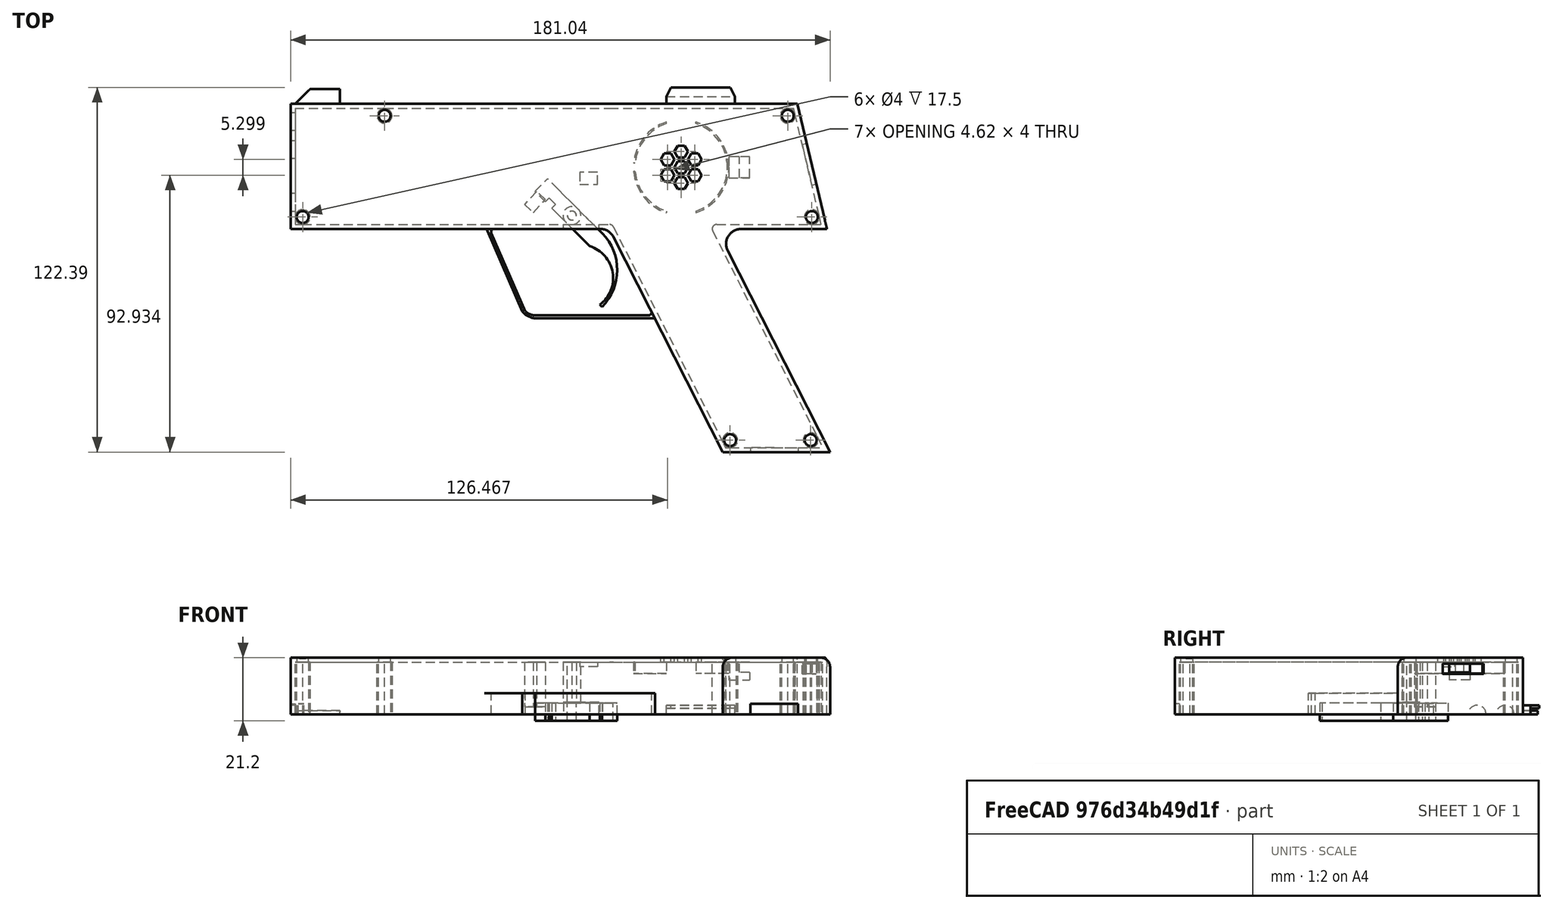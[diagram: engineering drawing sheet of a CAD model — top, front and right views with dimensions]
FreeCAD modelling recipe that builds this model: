
FCSTD DOCUMENT  (FreeCAD 0.21R33771 (Git))
Label: TaggerPart1
License: All rights reserved
LicenseURL: http://en.wikipedia.org/wiki/All_rights_reserved
objects: Sketcher::SketchObject×24, PartDesign::Pad×12, PartDesign::Pocket×12, PartDesign::Fillet×4, PartDesign::Body×2, PartDesign::Thickness×1, PartDesign::Hole×1, Part::Compound×1, App::MeasureDistance×1, App::Part×1
note: 87 computed .brp shape members not serialized (recipe doc carries the construction recipe); baked Part::Feature solids carry a one-line shape summary decoded from their .brp

FEATURE [Sketcher::SketchObject] Sketch
  FullyConstrained = false
  MapMode = 5
  Support = -> [XY_Plane]
  sketch-geometry (12):
    g0: LineSegment StartX=0 StartY=0 StartZ=0 EndX=107 EndY=0 EndZ=0
    g1: LineSegment StartX=0 StartY=0 StartZ=0 EndX=0 EndY=-42 EndZ=0
    g2: LineSegment StartX=0 StartY=-42 StartZ=0 EndX=107 EndY=-42 EndZ=0
    g3: LineSegment StartX=107 StartY=0 StartZ=0 EndX=107 EndY=-42 EndZ=0
    g4: LineSegment StartX=107 StartY=0 StartZ=0 EndX=170 EndY=0 EndZ=0
    g5: LineSegment StartX=107 StartY=-42 StartZ=0 EndX=143 EndY=-42 EndZ=0
    g6: LineSegment StartX=107 StartY=-42 StartZ=0 EndX=145.042 EndY=-116.892 EndZ=0
    g7: LineSegment StartX=143 StartY=-42 StartZ=0 EndX=181.042 EndY=-116.892 EndZ=0
    g8: LineSegment StartX=145.042 StartY=-116.892 StartZ=0 EndX=181.042 EndY=-116.892 EndZ=0
    g9: LineSegment StartX=143 StartY=-42 StartZ=0 EndX=180 EndY=-42 EndZ=0
    g10: LineSegment StartX=180 StartY=-42 StartZ=0 EndX=170 EndY=0 EndZ=0
    g11: LineSegment StartX=170 StartY=0 StartZ=0 EndX=170 EndY=-42 EndZ=0
  constraints (32):
    c: Coincident(g0,g-1)
    c: PointOnObject(g0,g-1)
    c: Coincident(g1,g0)
    c: PointOnObject(g1,g-2)
    c: Coincident(g2,g1)
    c: Horizontal(g2)
    c: Coincident(g3,g0)
    c: Coincident(g3,g2)
    c: Vertical(g3)
    c: Coincident(g4,g0)
    c: PointOnObject(g4,g-1)
    c: Coincident(g5,g2)
    c: Horizontal(g5)
    c: Coincident(g6,g2)
    c: Coincident(g7,g5)
    c: Coincident(g8,g6)
    c: Coincident(g8,g7)
    c: Horizontal(g8)
    c: Coincident(g9,g7)
    c: Horizontal(g9)
    c: Coincident(g10,g9)
    c: Coincident(g10,g4)
    c: Coincident(g11,g4)
    c: PointOnObject(g11,g9)
    c: Vertical(g11)
    c: DistanceY(g1,g1) = 42
    c: DistanceX(g1,g9) = 180
    c: DistanceX(g0,g4) = 170
    c: Parallel(g7,g6)
    c: Distance(g7) = 84
    c: DistanceX(g5,g5) = 36
    c: DistanceX(g9,g9) = 37
FEATURE [Sketcher::SketchObject] Sketch001  label="Triggerumrahmung"
  ExternalGeometry = -> [Sketch]
  FullyConstrained = false
  MapMode = 5
  Support = -> [XY_Plane]
  sketch-geometry (16):
    g0: LineSegment StartX=107 StartY=-42 StartZ=0 EndX=107 EndY=-71 EndZ=0
    g1: LineSegment StartX=107 StartY=-71 StartZ=0 EndX=121.731 EndY=-71 EndZ=0
    g2: LineSegment StartX=107 StartY=-71 StartZ=0 EndX=66.7308 EndY=-71 EndZ=0
    g3: LineSegment StartX=66.7308 StartY=-71 StartZ=0 EndX=66.7308 EndY=-42 EndZ=0
    g4: LineSegment StartX=121.731 StartY=-71 StartZ=0 EndX=81.9929 EndY=-71 EndZ=0
    g5: LineSegment StartX=78.7821 StartY=-69.7248 StartZ=0 EndX=66.7308 EndY=-42 EndZ=0
    g6: ArcOfCircle CenterX=82.1691 CenterY=-65.8766 CenterZ=0 NormalX=0 NormalY=0 NormalZ=1 AngleXU=0 Radius=5.12641 StartAngle=3.99065 EndAngle=4.678
    g7: LineSegment StartX=121.731 StartY=-71 StartZ=0 EndX=121.731 EndY=-72 EndZ=0
    g8: LineSegment StartX=121.731 StartY=-72 StartZ=0 EndX=81.9929 EndY=-72 EndZ=0
    g9: LineSegment StartX=81.9929 StartY=-71 StartZ=0 EndX=81.9929 EndY=-72 EndZ=0
    g10: ArcOfCircle CenterX=82.7291 CenterY=-65.6034 CenterZ=0 NormalX=0 NormalY=0 NormalZ=1 AngleXU=0 Radius=6.43882 StartAngle=3.8362 EndAngle=4.59779
    g11: LineSegment StartX=66.7308 StartY=-42 StartZ=0 EndX=65.7308 EndY=-42 EndZ=0
    g12: LineSegment StartX=65.7308 StartY=-42 StartZ=0 EndX=77.7821 EndY=-69.7248 EndZ=0
    g13: LineSegment StartX=78.7821 StartY=-69.7248 StartZ=0 EndX=77.7821 EndY=-69.7248 EndZ=0
    g14: LineSegment StartX=121.731 StartY=-72 StartZ=0 EndX=122.239 EndY=-72 EndZ=0
    g15: LineSegment StartX=122.239 StartY=-72 StartZ=0 EndX=121.731 EndY=-71 EndZ=0
  constraints (44):
    c: Coincident(g0,g-4)
    c: Vertical(g0)
    c: DistanceY(g0,g0) = 29
    c: PointOnObject(g1,g-3)
    c: Horizontal(g1)
    c: Coincident(g1,g0)
    c: Coincident(g2,g0)
    c: Horizontal(g2)
    c: DistanceX(g2,g1) = 55
    c: Coincident(g3,g2)
    c: PointOnObject(g3,g-4)
    c: Vertical(g3)
    c: Coincident(g4,g1)
    c: Coincident(g5,g3)
    c: Horizontal(g4)
    c: Coincident(g6,g5)
    c: Coincident(g6,g4)
    c: Coincident(g7,g4)
    c: Vertical(g7)
    c: Coincident(g8,g7)
    c: Horizontal(g8)
    c: Coincident(g9,g4)
    c: Coincident(g9,g8)
    c: Vertical(g9)
    c: DistanceY(g9,g9) = 1
    c: Coincident(g10,g8)
    c: Coincident(g11,g5)
    c: PointOnObject(g11,g-4)
    c: DistanceX(g11,g11) = 1
    c: Coincident(g12,g11)
    c: Coincident(g12,g10)
    c: DistanceX(g6) = 82.1691
    c: DistanceY(g6) = -65.8766
    c: Equal(g12,g5)
    c: Coincident(g13,g5)
    c: Horizontal(g13)
    c: Coincident(g10,g13)
    c: DistanceX(g4) = 81.9929
    c: DistanceX(g5) = 78.7821
    c: Coincident(g14,g8)
    c: PointOnObject(g14,g-3)
    c: Horizontal(g14)
    c: Coincident(g15,g14)
    c: Coincident(g15,g4)
FEATURE [Sketcher::SketchObject] Sketch002  label="Kim2"
  AttachmentOffset = pos=(0,0,2) rot=(0,0,1;0rad)
  ExternalGeometry = -> [Sketch]
  FullyConstrained = false
  MapMode = 5
  Placement = pos=(0,0,2) rot=(0,0,1;0rad)
  Support = -> [XY_Plane]
  sketch-geometry (10):
    g0: LineSegment StartX=170 StartY=0 StartZ=0 EndX=170 EndY=-42 EndZ=0
    g1: LineSegment StartX=149.115 StartY=0 StartZ=0 EndX=149.115 EndY=2.5 EndZ=0
    g2: LineSegment StartX=149.115 StartY=2.5 StartZ=0 EndX=147.523 EndY=5.5 EndZ=0
    g3: LineSegment StartX=147.523 StartY=5.5 StartZ=0 EndX=127.662 EndY=5.5 EndZ=0
    g4: LineSegment StartX=127.662 StartY=5.5 StartZ=0 EndX=126.07 EndY=2.5 EndZ=0
    g5: LineSegment StartX=126.07 StartY=2.5 StartZ=0 EndX=126.07 EndY=0 EndZ=0
    g6: LineSegment StartX=126.07 StartY=2.5 StartZ=0 EndX=149.115 EndY=2.5 EndZ=0
    g7: LineSegment StartX=127.662 StartY=5.5 StartZ=0 EndX=127.662 EndY=2.5 EndZ=0
    g8: LineSegment StartX=147.523 StartY=5.5 StartZ=0 EndX=147.523 EndY=2.5 EndZ=0
    g9: LineSegment StartX=126.07 StartY=0 StartZ=0 EndX=149.115 EndY=0 EndZ=0
  constraints (26):
    c: Coincident(g0,g-6)
    c: PointOnObject(g0,g-7)
    c: Vertical(g0)
    c: PointOnObject(g1,g-4)
    c: Vertical(g1)
    c: Coincident(g3,g2)
    c: Horizontal(g3)
    c: Coincident(g4,g3)
    c: Coincident(g5,g4)
    c: PointOnObject(g5,g-4)
    c: Equal(g5,g1)
    c: Equal(g4,g2)
    c: Coincident(g2,g1)
    c: Vertical(g5)
    c: Coincident(g6,g4)
    c: Coincident(g6,g1)
    c: Coincident(g7,g3)
    c: PointOnObject(g7,g6)
    c: Vertical(g7)
    c: Coincident(g8,g2)
    c: PointOnObject(g8,g6)
    c: Vertical(g8)
    c: DistanceY(g8,g8) = 3
    c: DistanceY(g5,g3) = 5.5
    c: Coincident(g9,g5)
    c: Coincident(g9,g1)
FEATURE [Sketcher::SketchObject] Sketch003  label="Korn"
  ExternalGeometry = -> [Sketch,Sketch002]
  FullyConstrained = false
  MapMode = 5
  Support = -> [XY_Plane]
  sketch-geometry (7):
    g0: LineSegment StartX=1.52333 StartY=0 StartZ=0 EndX=6.52333 EndY=5 EndZ=0
    g1: LineSegment StartX=6.52333 StartY=5 StartZ=0 EndX=16.5233 EndY=5 EndZ=0
    g2: LineSegment StartX=16.5233 StartY=5 StartZ=0 EndX=16.5233 EndY=0 EndZ=0
    g3: LineSegment StartX=16.5233 StartY=0 StartZ=0 EndX=1.52333 EndY=0 EndZ=0
    g4: LineSegment StartX=127.662 StartY=5.5 StartZ=0 EndX=127.662 EndY=0 EndZ=0
    g5: LineSegment StartX=6.52333 StartY=5 StartZ=0 EndX=6.52333 EndY=0 EndZ=0
    g6: LineSegment StartX=1.52333 StartY=0 StartZ=0 EndX=1.52333 EndY=-1.50251 EndZ=0
  constraints (19):
    c: Coincident(g1,g0)
    c: Horizontal(g1)
    c: Coincident(g2,g1)
    c: PointOnObject(g2,g-3)
    c: Coincident(g3,g2)
    c: Coincident(g3,g0)
    c: Vertical(g2)
    c: Coincident(g4,g-6)
    c: PointOnObject(g4,g-8)
    c: Vertical(g4)
    c: DistanceY(g2,g2) = 5
    c: Coincident(g5,g0)
    c: PointOnObject(g5,g3)
    c: Vertical(g5)
    c: Angle(g0,g5) = 0.785398
    c: DistanceX(g3,g3) = 15
    c: PointOnObject(g0,g-3)
    c: Coincident(g6,g0)
    c: Vertical(g6)
FEATURE [PartDesign::Pad] Pad
  Direction = (0,0,1)
  Length = 19
  Length2 = 10
  Profile = -> Sketch
  ReferenceAxis = -> Sketch [N_Axis]
  Type = 0
FEATURE [PartDesign::Thickness] Thickness
  Base = -> Pad [Face10]
  BaseFeature = -> Pad
  Intersection = false
  Join = 0
  Mode = 0
  Reversed = true
  SupportTransform = false
  Value = 1.5
FEATURE [Sketcher::SketchObject] Sketch004  label="Kim1"
  ExternalGeometry = -> [Sketch002]
  FullyConstrained = true
  MapMode = 5
  Support = -> [XY_Plane]
  sketch-geometry (4):
    g0: LineSegment StartX=126.07 StartY=2.5 StartZ=0 EndX=149.115 EndY=2.5 EndZ=0
    g1: LineSegment StartX=149.115 StartY=2.5 StartZ=0 EndX=149.115 EndY=0 EndZ=0
    g2: LineSegment StartX=149.115 StartY=0 StartZ=0 EndX=126.07 EndY=0 EndZ=0
    g3: LineSegment StartX=126.07 StartY=0 StartZ=0 EndX=126.07 EndY=2.5 EndZ=0
  constraints (8):
    c: Coincident(g0,g-5)
    c: Coincident(g0,g-7)
    c: Coincident(g1,g0)
    c: Coincident(g1,g-8)
    c: Coincident(g2,g-8)
    c: Coincident(g3,g0)
    c: Coincident(g2,g1)
    c: Coincident(g3,g2)
FEATURE [PartDesign::Pad] Pad001
  BaseFeature = -> Thickness
  Direction = (0,0,1)
  Length = 2
  Length2 = 10
  Profile = -> Sketch004
  ReferenceAxis = -> Sketch004 [N_Axis]
  Type = 0
FEATURE [PartDesign::Pad] Pad002
  BaseFeature = -> Pad001
  Direction = (0,0,1)
  Length = 1
  Length2 = 10
  Profile = -> Sketch002
  ReferenceAxis = -> Sketch002 [N_Axis]
  Type = 0
FEATURE [PartDesign::Pad] Pad003
  BaseFeature = -> Pad002
  Direction = (0,0,1)
  Length = 1.2
  Length2 = 10
  Profile = -> Sketch003
  ReferenceAxis = -> Sketch003 [N_Axis]
  Type = 0
FEATURE [PartDesign::Fillet] Fillet
  Base = -> Pad003 [Edge93]
  BaseFeature = -> Pad003
  Radius = 0.5
  SupportTransform = false
  UseAllEdges = false
FEATURE [PartDesign::Pad] Pad004
  BaseFeature = -> Fillet
  Direction = (0,0,1)
  Length = 7
  Length2 = 10
  Profile = -> Sketch001
  ReferenceAxis = -> Sketch001 [N_Axis]
  Type = 0
FEATURE [Sketcher::SketchObject] Sketch005  label="laserlöcher"
  ExternalGeometry = -> [Pad004]
  FullyConstrained = true
  MapMode = 5
  Placement = pos=(1.5,0,0) rot=(0.57735,0.57735,0.57735;2.0944rad)
  Support = -> [Pad004]
  sketch-geometry (6):
    g0: LineSegment StartX=-12.3 StartY=0 StartZ=0 EndX=0 EndY=0 EndZ=0
    g1: ArcOfCircle CenterX=-15.4 CenterY=0 CenterZ=0 NormalX=0 NormalY=0 NormalZ=1 AngleXU=0 Radius=3.1 StartAngle=0 EndAngle=3.14159
    g2: LineSegment StartX=-18.5 StartY=-1e-15 StartZ=0 EndX=-12.3 EndY=0 EndZ=0
    g3: ArcOfCircle CenterX=-6 CenterY=0 CenterZ=0 NormalX=0 NormalY=0 NormalZ=1 AngleXU=0 Radius=3.3 StartAngle=0 EndAngle=3.14159
    g4: LineSegment StartX=-9.3 StartY=0 StartZ=0 EndX=-2.7 EndY=0 EndZ=0
    g5: LineSegment StartX=-40.5 StartY=-1e-15 StartZ=0 EndX=-18.5 EndY=-1e-15 EndZ=0
  constraints (18):
    c: Radius(g1) = 3.1
    c: Coincident(g2,g1)
    c: Coincident(g2,g1)
    c: Coincident(g0,g-1)
    c: PointOnObject(g3,g0)
    c: PointOnObject(g3,g0)
    c: PointOnObject(g3,g0)
    c: Radius(g3) = 3.3
    c: Coincident(g4,g3)
    c: Coincident(g4,g3)
    c: DistanceX(g1,g3) = 3
    c: Coincident(g5,g-3)
    c: Coincident(g5,g1)
    c: Horizontal(g5)
    c: DistanceX(g5,g5) = 22
    c: Coincident(g0,g1)
    c: Horizontal(g0)
    c: PointOnObject(g1,g2)
FEATURE [Sketcher::SketchObject] Sketch006  label="Schraubenlöcher"
  ExternalGeometry = -> [Pad004]
  FullyConstrained = false
  MapMode = 5
  Placement = pos=(0,0,17.5) rot=(1,0,0;3.14159rad)
  Support = -> [Pad004]
  sketch-geometry (20):
    g0: Circle CenterX=31.5 CenterY=4 CenterZ=0 NormalX=0 NormalY=0 NormalZ=1 AngleXU=0 Radius=2
    g1: Circle CenterX=31.5 CenterY=4 CenterZ=0 NormalX=0 NormalY=0 NormalZ=1 AngleXU=0 Radius=2.5
    g2: Circle CenterX=4 CenterY=38 CenterZ=0 NormalX=0 NormalY=0 NormalZ=1 AngleXU=0 Radius=2.5
    g3: Circle CenterX=4 CenterY=38 CenterZ=0 NormalX=0 NormalY=0 NormalZ=1 AngleXU=0 Radius=2
    g4: Circle CenterX=147.497 CenterY=112.892 CenterZ=0 NormalX=0 NormalY=0 NormalZ=1 AngleXU=0 Radius=2
    g5: Circle CenterX=147.497 CenterY=112.892 CenterZ=0 NormalX=0 NormalY=0 NormalZ=1 AngleXU=0 Radius=2.5
    g6: Circle CenterX=166.841 CenterY=4 CenterZ=0 NormalX=0 NormalY=0 NormalZ=1 AngleXU=0 Radius=2
    g7: Circle CenterX=166.841 CenterY=4 CenterZ=0 NormalX=0 NormalY=0 NormalZ=1 AngleXU=0 Radius=2.5
    g8: Circle CenterX=174.524 CenterY=112.892 CenterZ=0 NormalX=0 NormalY=0 NormalZ=1 AngleXU=0 Radius=2
    g9: Circle CenterX=174.524 CenterY=112.892 CenterZ=0 NormalX=0 NormalY=0 NormalZ=1 AngleXU=0 Radius=2.5
    g10: Circle CenterX=174.936 CenterY=38 CenterZ=0 NormalX=0 NormalY=0 NormalZ=1 AngleXU=0 Radius=2
    g11: Circle CenterX=174.936 CenterY=38 CenterZ=0 NormalX=0 NormalY=0 NormalZ=1 AngleXU=0 Radius=2.5
    g12: GeomPoint X=166.841 Y=1.5 Z=0
    g13: GeomPoint X=169.273 Y=3.42095 Z=0
    g14: GeomPoint X=174.936 Y=40.5 Z=0
    g15: GeomPoint X=177.368 Y=37.4209 Z=0
    g16: GeomPoint X=147.497 Y=115.392 Z=0
    g17: GeomPoint X=145.268 Y=114.024 Z=0
    g18: GeomPoint X=31.5 Y=1.5 Z=0
    g19: GeomPoint X=1.5 Y=3.78568 Z=0
  constraints (39):
    c: Coincident(g1,g0)
    c: Coincident(g3,g2)
    c: Equal(g3,g0)
    c: Tangent(g-5,g2)
    c: Tangent(g2,g-6)
    c: Radius(g2) = 2.5
    c: Radius(g3) = 2
    c: Coincident(g5,g4)
    c: Radius(g5) = 2.5
    c: Radius(g4) = 2
    c: Coincident(g7,g6)
    c: Radius(g6) = 2
    c: Coincident(g9,g8)
    c: Radius(g8) = 2
    c: Radius(g9) = 2.5
    c: Tangent(g9,g-8)
    c: Tangent(g9,g-7)
    c: Coincident(g11,g10)
    c: Radius(g11) = 2.5
    c: Radius(g7) = 2.5
    c: PointOnObject(g12,g7)
    c: PointOnObject(g13,g7)
    c: PointOnObject(g12,g-9)
    c: PointOnObject(g13,g-3)
    c: Radius(g10) = 2
    c: PointOnObject(g14,g11)
    c: PointOnObject(g15,g11)
    c: PointOnObject(g14,g-10)
    c: PointOnObject(g15,g-3)
    c: Radius(g1) = 2.5
    c: PointOnObject(g16,g5)
    c: PointOnObject(g17,g5)
    c: PointOnObject(g16,g-8)
    c: PointOnObject(g17,g-11)
    c: PointOnObject(g18,g1)
    c: PointOnObject(g18,g-4)
    c: DistanceX(g-6,g-6) = 0
    c: PointOnObject(g19,g-6)
    c: DistanceX(g19,g0) = 30
FEATURE [PartDesign::Pad] Pad005
  BaseFeature = -> Pad004
  Direction = (0,0,-1)
  Length = 17.5
  Length2 = 10
  Profile = -> Sketch006
  ReferenceAxis = -> Sketch006 [N_Axis]
  Type = 0
FEATURE [Sketcher::SketchObject] Sketch007  label="Triggerausschnitt"
  ExternalGeometry = -> [Pad005]
  FullyConstrained = true
  MapMode = 5
  Placement = pos=(0,-42,0) rot=(1,0,0;1.5708rad)
  Support = -> [Pad005]
  sketch-geometry (4):
    g0: LineSegment StartX=103.5 StartY=0 StartZ=0 EndX=103.5 EndY=4 EndZ=0
    g1: LineSegment StartX=103.5 StartY=4 StartZ=0 EndX=91.5 EndY=4 EndZ=0
    g2: LineSegment StartX=91.5 StartY=4 StartZ=0 EndX=91.5 EndY=0 EndZ=0
    g3: LineSegment StartX=91.5 StartY=0 StartZ=0 EndX=103.5 EndY=0 EndZ=0
  constraints (12):
    c: PointOnObject(g0,g-3)
    c: Vertical(g0)
    c: Coincident(g1,g0)
    c: Horizontal(g1)
    c: Coincident(g2,g1)
    c: PointOnObject(g2,g-3)
    c: Vertical(g2)
    c: DistanceY(g2,g2) = 4
    c: Coincident(g3,g2)
    c: Coincident(g3,g0)
    c: DistanceX(g1,g0) = 12
    c: DistanceX(g0,g-3) = 3.5
FEATURE [PartDesign::Pocket] Pocket
  BaseFeature = -> Pad005
  Direction = (0,1,-2e-16)
  Length = 5
  Length2 = 5
  Profile = -> Sketch007
  ReferenceAxis = -> Sketch007 [N_Axis]
  Type = 0
FEATURE [PartDesign::Hole] Hole
  BaseFeature = -> Pocket
  CustomThreadClearance = 0
  Depth = 25
  DepthType = 0
  Diameter = 6
  DrillForDepth = false
  DrillPoint = 1
  DrillPointAngle = 118
  HoleCutCountersinkAngle = 90
  HoleCutCustomValues = false
  HoleCutDepth = 0
  HoleCutDiameter = 6.1
  HoleCutType = 0
  ModelThread = false
  Profile = -> Sketch005
  Tapered = false
  TaperedAngle = 90
  ThreadClass = 0
  ThreadDepth = 25
  ThreadDepthType = 0
  ThreadDirection = 0
  ThreadFit = 0
  ThreadSize = 0
  ThreadType = 0
  Threaded = false
  UseCustomThreadClearance = false
FEATURE [Sketcher::SketchObject] Sketch010  label="Datenkabelloch"
  FullyConstrained = false
  MapMode = 5
  Placement = pos=(0,-115.392,0) rot=(0,0.707107,0.707107;3.14159rad)
  sketch-geometry (10):
    g0: LineSegment StartX=-178.598 StartY=11.5 StartZ=0 EndX=-174.524 EndY=11.5 EndZ=0
    g1: LineSegment StartX=-147.497 StartY=11.5 StartZ=0 EndX=-145.963 EndY=11.5 EndZ=0
    g2: LineSegment StartX=-178.598 StartY=0 StartZ=0 EndX=-162.28 EndY=0 EndZ=0
    g3: LineSegment StartX=-162.28 StartY=0 StartZ=0 EndX=-145.963 EndY=0 EndZ=0
    g4: LineSegment StartX=-162.28 StartY=0 StartZ=0 EndX=-162.28 EndY=3.5 EndZ=0
    g5: LineSegment StartX=-162.28 StartY=3.5 StartZ=0 EndX=-154.28 EndY=3.5 EndZ=0
    g6: LineSegment StartX=-162.28 StartY=3.5 StartZ=0 EndX=-170.28 EndY=3.5 EndZ=0
    g7: LineSegment StartX=-170.28 StartY=3.5 StartZ=0 EndX=-170.28 EndY=3.73e-14 EndZ=0
    g8: LineSegment StartX=-154.28 StartY=3.5 StartZ=0 EndX=-154.28 EndY=-3.86e-14 EndZ=0
    g9: LineSegment StartX=-154.28 StartY=-3.86e-14 StartZ=0 EndX=-170.28 EndY=3.74e-14 EndZ=0
  constraints (19):
    c: Coincident(g3,g2)
    c: Equal(g2,g3)
    c: Coincident(g4,g2)
    c: Vertical(g4)
    c: DistanceY(g4,g4) = 3.5
    c: Coincident(g5,g4)
    c: Horizontal(g5)
    c: Coincident(g6,g5)
    c: Equal(g6,g5)
    c: Horizontal(g6)
    c: DistanceX(g5,g5) = 8
    c: Coincident(g7,g6)
    c: PointOnObject(g7,g2)
    c: Vertical(g7)
    c: Coincident(g8,g5)
    c: PointOnObject(g8,g3)
    c: Vertical(g8)
    c: Coincident(g9,g8)
    c: Coincident(g9,g7)
FEATURE [PartDesign::Pocket] Pocket001
  BaseFeature = -> Hole
  Direction = (0,-1,2e-16)
  Length = 5
  Length2 = 5
  Profile = -> Sketch010
  ReferenceAxis = -> Sketch010 [N_Axis]
  Type = 0
FEATURE [Sketcher::SketchObject] Sketch011  label="Lautsprecherbefestigung"
  ExternalGeometry = -> [Pocket001]
  FullyConstrained = false
  MapMode = 5
  Placement = pos=(0,0,17.5) rot=(1,0,0;3.14159rad)
  Support = -> [Pocket001]
  sketch-geometry (7):
    g0: Circle CenterX=131.056 CenterY=21.3061 CenterZ=0 NormalX=0 NormalY=0 NormalZ=1 AngleXU=0 Radius=15.5
    g1: Circle CenterX=131.056 CenterY=21.3061 CenterZ=0 NormalX=0 NormalY=0 NormalZ=1 AngleXU=0 Radius=16
    g2: LineSegment StartX=131.056 StartY=21.3061 StartZ=0 EndX=131.056 EndY=1.5 EndZ=0
    g3: LineSegment StartX=131.056 StartY=21.3061 StartZ=0 EndX=143 EndY=40.5 EndZ=0
    g4: LineSegment StartX=143 StartY=42 StartZ=0 EndX=131.056 EndY=21.3061 EndZ=0
    g5: LineSegment StartX=141.678 StartY=42.7087 StartZ=0 EndX=131.056 EndY=21.3061 EndZ=0
    g6: LineSegment StartX=131.056 StartY=21.3061 StartZ=0 EndX=147.497 EndY=112.892 EndZ=0
  constraints (14):
    c: Coincident(g1,g0)
    c: Radius(g1) = 16
    c: Radius(g0) = 15.5
    c: Coincident(g2,g0)
    c: PointOnObject(g2,g-3)
    c: Vertical(g2)
    c: Coincident(g3,g0)
    c: Coincident(g3,g-8)
    c: Coincident(g4,g0)
    c: Coincident(g5,g0)
    c: Equal(g5,g4)
    c: Coincident(g6,g0)
    c: DistanceX(g0) = 131.056
    c: DistanceY(g0) = 21.3061
FEATURE [Sketcher::SketchObject] Sketch012  label="Lautsprecherbefestigung-optimierungen"
  ExternalGeometry = -> [Sketch011]
  FullyConstrained = true
  MapMode = 5
  Placement = pos=(0,0,17.5) rot=(1,0,0;3.14159rad)
  Support = -> [Pocket001]
  sketch-geometry (21):
    g0: ArcOfCircle CenterX=131.056 CenterY=21.3061 CenterZ=0 NormalX=0 NormalY=0 NormalZ=1 AngleXU=0 Radius=15.5 StartAngle=1.24234 EndAngle=1.89925
    g1: LineSegment StartX=126.056 StartY=35.9775 StartZ=0 EndX=131.056 EndY=35.9775 EndZ=0
    g2: LineSegment StartX=131.056 StartY=35.9775 StartZ=0 EndX=136.056 EndY=35.9775 EndZ=0
    g3: LineSegment StartX=131.056 StartY=35.9775 StartZ=0 EndX=131.056 EndY=21.3061 EndZ=0
    g4: LineSegment StartX=126.056 StartY=35.9775 StartZ=0 EndX=126.056 EndY=36.5048 EndZ=0
    g5: LineSegment StartX=136.056 StartY=35.9775 StartZ=0 EndX=136.056 EndY=36.5048 EndZ=0
    g6: ArcOfCircle CenterX=131.056 CenterY=21.3061 CenterZ=0 NormalX=0 NormalY=0 NormalZ=1 AngleXU=0 Radius=16 StartAngle=1.25297 EndAngle=1.88862
    g7: ArcOfCircle CenterX=131.056 CenterY=21.3061 CenterZ=0 NormalX=0 NormalY=0 NormalZ=1 AngleXU=0 Radius=15.5 StartAngle=4.38393 EndAngle=5.04084
    g8: LineSegment StartX=126.056 StartY=6.63469 StartZ=0 EndX=131.056 EndY=6.63469 EndZ=0
    g9: LineSegment StartX=131.056 StartY=6.63469 StartZ=0 EndX=136.056 EndY=6.63469 EndZ=0
    g10: LineSegment StartX=126.056 StartY=6.63469 StartZ=0 EndX=126.056 EndY=6.10741 EndZ=0
    g11: LineSegment StartX=136.056 StartY=6.63469 StartZ=0 EndX=136.056 EndY=6.10741 EndZ=0
    g12: ArcOfCircle CenterX=131.056 CenterY=21.3061 CenterZ=0 NormalX=0 NormalY=0 NormalZ=1 AngleXU=0 Radius=16 StartAngle=4.39457 EndAngle=5.03021
    g13: LineSegment StartX=131.056 StartY=6.63469 StartZ=0 EndX=131.056 EndY=21.3061 EndZ=0
    g14: ArcOfCircle CenterX=131.056 CenterY=21.3061 CenterZ=0 NormalX=0 NormalY=0 NormalZ=1 AngleXU=0 Radius=15.5 StartAngle=3.05115 EndAngle=3.23204
    g15: LineSegment StartX=115.619 StartY=22.7061 StartZ=0 EndX=115.619 EndY=21.3061 EndZ=0
    g16: LineSegment StartX=115.619 StartY=21.3061 StartZ=0 EndX=115.619 EndY=19.9061 EndZ=0
    g17: LineSegment StartX=115.619 StartY=21.3061 StartZ=0 EndX=131.056 EndY=21.3061 EndZ=0
    g18: LineSegment StartX=115.619 StartY=22.7061 StartZ=0 EndX=115.117 EndY=22.7061 EndZ=0
    g19: LineSegment StartX=115.619 StartY=19.9061 StartZ=0 EndX=115.117 EndY=19.9061 EndZ=0
    g20: ArcOfCircle CenterX=131.056 CenterY=21.3061 CenterZ=0 NormalX=0 NormalY=0 NormalZ=1 AngleXU=0 Radius=16 StartAngle=3.05398 EndAngle=3.2292
  constraints (57):
    c: Coincident(g6,g5)
    c: Coincident(g0,g5)
    c: Vertical(g5)
    c: Vertical(g4)
    c: Coincident(g6,g4)
    c: Coincident(g4,g0)
    c: Coincident(g2,g1)
    c: Coincident(g1,g3)
    c: Horizontal(g1)
    c: Horizontal(g2)
    c: Vertical(g3)
    c: DistanceX(g2,g2) = 5
    c: Coincident(g1,g0)
    c: PointOnObject(g5,g-3)
    c: Coincident(g6,g-4)
    c: Coincident(g6,g3)
    c: Coincident(g6,g0)
    c: Coincident(g0,g2)
    c: PointOnObject(g0,g-4)
    c: Coincident(g7,g0)
    c: PointOnObject(g7,g-4)
    c: Coincident(g8,g7)
    c: Horizontal(g8)
    c: Coincident(g9,g8)
    c: Coincident(g9,g7)
    c: Horizontal(g9)
    c: Equal(g9,g8)
    c: DistanceX(g8,g8) = 5
    c: Coincident(g10,g7)
    c: PointOnObject(g10,g-3)
    c: Vertical(g10)
    c: Coincident(g11,g7)
    c: Coincident(g12,g0)
    c: Coincident(g12,g10)
    c: Coincident(g12,g11)
    c: Coincident(g13,g8)
    c: Coincident(g13,g0)
    c: Coincident(g14,g0)
    c: PointOnObject(g14,g-4)
    c: Coincident(g15,g14)
    c: Vertical(g15)
    c: Coincident(g16,g15)
    c: Coincident(g16,g14)
    c: Vertical(g16)
    c: Vertical(g11)
    c: Equal(g16,g15)
    c: Coincident(g17,g15)
    c: Coincident(g17,g0)
    c: Coincident(g18,g14)
    c: PointOnObject(g18,g-3)
    c: Horizontal(g18)
    c: Coincident(g19,g14)
    c: Horizontal(g19)
    c: Coincident(g20,g0)
    c: Coincident(g20,g19)
    c: Coincident(g20,g18)
    c: DistanceY(g15,g15) = 1.4
FEATURE [Sketcher::SketchObject] Sketch013  label="Sechsecke-Loch"
  ExternalGeometry = -> [Sketch011,Sketch012]
  FullyConstrained = true
  MapMode = 5
  Placement = pos=(0,0,17.5) rot=(1,0,0;3.14159rad)
  Support = -> [Pocket001]
  sketch-geometry (65):
    g0: LineSegment StartX=131.056 StartY=21.3061 StartZ=0 EndX=131.056 EndY=23.3061 EndZ=0
    g1: LineSegment StartX=131.056 StartY=21.3061 StartZ=0 EndX=131.056 EndY=19.3061 EndZ=0
    g2: LineSegment StartX=131.056 StartY=23.3061 StartZ=0 EndX=132.21 EndY=23.3061 EndZ=0
    g3: LineSegment StartX=131.056 StartY=23.3061 StartZ=0 EndX=129.901 EndY=23.3061 EndZ=0
    g4: LineSegment StartX=129.901 StartY=23.3061 StartZ=0 EndX=128.746 EndY=21.3061 EndZ=0
    g5: LineSegment StartX=131.056 StartY=19.3061 StartZ=0 EndX=132.21 EndY=19.3061 EndZ=0
    g6: LineSegment StartX=131.056 StartY=19.3061 StartZ=0 EndX=129.901 EndY=19.3061 EndZ=0
    g7: LineSegment StartX=129.901 StartY=19.3061 StartZ=0 EndX=128.746 EndY=21.3061 EndZ=0
    g8: LineSegment StartX=132.21 StartY=19.3061 StartZ=0 EndX=133.365 EndY=21.3061 EndZ=0
    g9: LineSegment StartX=133.365 StartY=21.3061 StartZ=0 EndX=132.21 EndY=23.3061 EndZ=0
    g10: LineSegment StartX=129.901 StartY=19.3061 StartZ=0 EndX=132.21 EndY=19.3061 EndZ=0
    g11: LineSegment StartX=129.901 StartY=19.3061 StartZ=0 EndX=129.151 EndY=18.0071 EndZ=0
    g12: LineSegment StartX=132.21 StartY=19.3061 StartZ=0 EndX=132.96 EndY=18.0071 EndZ=0
    g13: LineSegment StartX=133.365 StartY=21.3061 StartZ=0 EndX=134.865 EndY=21.3061 EndZ=0
    g14: LineSegment StartX=132.21 StartY=23.3061 StartZ=0 EndX=132.96 EndY=24.6051 EndZ=0
    g15: LineSegment StartX=129.901 StartY=23.3061 StartZ=0 EndX=129.151 EndY=24.6051 EndZ=0
    g16: LineSegment StartX=128.746 StartY=21.3061 StartZ=0 EndX=127.246 EndY=21.3061 EndZ=0
    g17: LineSegment StartX=132.96 StartY=18.0071 StartZ=0 EndX=132.21 EndY=18.0071 EndZ=0
    g18: LineSegment StartX=129.151 StartY=18.0071 StartZ=0 EndX=129.901 EndY=18.0071 EndZ=0
    g19: LineSegment StartX=129.901 StartY=18.0071 StartZ=0 EndX=132.21 EndY=18.0071 EndZ=0
    g20: LineSegment StartX=129.901 StartY=18.0071 StartZ=0 EndX=128.746 EndY=16.0071 EndZ=0
    g21: LineSegment StartX=128.746 StartY=16.0071 StartZ=0 EndX=129.901 EndY=14.0071 EndZ=0
    g22: LineSegment StartX=129.901 StartY=14.0071 StartZ=0 EndX=132.21 EndY=14.0071 EndZ=0
    g23: LineSegment StartX=132.21 StartY=14.0071 StartZ=0 EndX=133.365 EndY=16.0071 EndZ=0
    g24: LineSegment StartX=133.365 StartY=16.0071 StartZ=0 EndX=132.21 EndY=18.0071 EndZ=0
    g25: LineSegment StartX=132.96 StartY=18.0071 StartZ=0 EndX=133.335 EndY=18.6566 EndZ=0
    g26: LineSegment StartX=134.865 StartY=21.3061 StartZ=0 EndX=134.49 EndY=20.6566 EndZ=0
    g27: LineSegment StartX=134.49 StartY=20.6566 StartZ=0 EndX=133.335 EndY=18.6566 EndZ=0
    g28: LineSegment StartX=134.865 StartY=21.3061 StartZ=0 EndX=134.49 EndY=21.9556 EndZ=0
    g29: LineSegment StartX=132.96 StartY=24.6051 StartZ=0 EndX=133.335 EndY=23.9556 EndZ=0
    g30: LineSegment StartX=133.335 StartY=23.9556 StartZ=0 EndX=134.49 EndY=21.9556 EndZ=0
    g31: LineSegment StartX=129.151 StartY=24.6051 StartZ=0 EndX=129.901 EndY=24.6051 EndZ=0
    g32: LineSegment StartX=132.96 StartY=24.6051 StartZ=0 EndX=132.21 EndY=24.6051 EndZ=0
    g33: LineSegment StartX=129.901 StartY=24.6051 StartZ=0 EndX=132.21 EndY=24.6051 EndZ=0
    g34: LineSegment StartX=129.151 StartY=24.6051 StartZ=0 EndX=128.776 EndY=23.9556 EndZ=0
    g35: LineSegment StartX=127.246 StartY=21.3061 StartZ=0 EndX=127.621 EndY=21.9556 EndZ=0
    g36: LineSegment StartX=128.776 StartY=23.9556 StartZ=0 EndX=127.621 EndY=21.9556 EndZ=0
    g37: LineSegment StartX=133.335 StartY=18.6566 StartZ=0 EndX=134.49 EndY=16.6566 EndZ=0
    g38: LineSegment StartX=134.49 StartY=16.6566 StartZ=0 EndX=136.8 EndY=16.6566 EndZ=0
    g39: LineSegment StartX=136.8 StartY=16.6566 StartZ=0 EndX=137.954 EndY=18.6566 EndZ=0
    g40: LineSegment StartX=137.954 StartY=18.6566 StartZ=0 EndX=136.8 EndY=20.6566 EndZ=0
    g41: LineSegment StartX=136.8 StartY=20.6566 StartZ=0 EndX=134.49 EndY=20.6566 EndZ=0
    g42: LineSegment StartX=134.49 StartY=21.9556 StartZ=0 EndX=136.8 EndY=21.9556 EndZ=0
    g43: LineSegment StartX=136.8 StartY=21.9556 StartZ=0 EndX=137.954 EndY=23.9556 EndZ=0
    g44: LineSegment StartX=137.954 StartY=23.9556 StartZ=0 EndX=136.8 EndY=25.9556 EndZ=0
    g45: LineSegment StartX=136.8 StartY=25.9556 StartZ=0 EndX=134.49 EndY=25.9556 EndZ=0
    g46: LineSegment StartX=134.49 StartY=25.9556 StartZ=0 EndX=133.335 EndY=23.9556 EndZ=0
    g47: LineSegment StartX=132.21 StartY=24.6051 StartZ=0 EndX=133.365 EndY=26.6051 EndZ=0
    g48: LineSegment StartX=133.365 StartY=26.6051 StartZ=0 EndX=132.21 EndY=28.6051 EndZ=0
    g49: LineSegment StartX=132.21 StartY=28.6051 StartZ=0 EndX=129.901 EndY=28.6051 EndZ=0
    g50: LineSegment StartX=129.901 StartY=28.6051 StartZ=0 EndX=128.746 EndY=26.6051 EndZ=0
    g51: LineSegment StartX=128.746 StartY=26.6051 StartZ=0 EndX=129.901 EndY=24.6051 EndZ=0
    g52: LineSegment StartX=127.621 StartY=21.9556 StartZ=0 EndX=125.312 EndY=21.9556 EndZ=0
    g53: LineSegment StartX=125.312 StartY=21.9556 StartZ=0 EndX=124.157 EndY=23.9556 EndZ=0
    g54: LineSegment StartX=124.157 StartY=23.9556 StartZ=0 EndX=125.312 EndY=25.9556 EndZ=0
    g55: LineSegment StartX=125.312 StartY=25.9556 StartZ=0 EndX=127.621 EndY=25.9556 EndZ=0
    g56: LineSegment StartX=127.621 StartY=25.9556 StartZ=0 EndX=128.776 EndY=23.9556 EndZ=0
    g57: LineSegment StartX=127.246 StartY=21.3061 StartZ=0 EndX=127.621 EndY=20.6566 EndZ=0
    g58: LineSegment StartX=129.151 StartY=18.0071 StartZ=0 EndX=128.776 EndY=18.6566 EndZ=0
    g59: LineSegment StartX=127.621 StartY=20.6566 StartZ=0 EndX=128.776 EndY=18.6566 EndZ=0
    g60: LineSegment StartX=128.776 StartY=18.6566 StartZ=0 EndX=127.621 EndY=16.6566 EndZ=0
    g61: LineSegment StartX=127.621 StartY=16.6566 StartZ=0 EndX=125.312 EndY=16.6566 EndZ=0
    g62: LineSegment StartX=125.312 StartY=16.6566 StartZ=0 EndX=124.157 EndY=18.6566 EndZ=0
    g63: LineSegment StartX=124.157 StartY=18.6566 StartZ=0 EndX=125.312 EndY=20.6566 EndZ=0
    g64: LineSegment StartX=125.312 StartY=20.6566 StartZ=0 EndX=127.621 EndY=20.6566 EndZ=0
  constraints (180):
    c: Coincident(g0,g-4)
    c: Vertical(g0)
    c: Coincident(g1,g0)
    c: Vertical(g1)
    c: Equal(g1,g0)
    c: Coincident(g2,g0)
    c: Horizontal(g2)
    c: Coincident(g3,g2)
    c: Horizontal(g3)
    c: Coincident(g4,g3)
    c: Coincident(g5,g1)
    c: Horizontal(g5)
    c: Coincident(g6,g5)
    c: Horizontal(g6)
    c: Coincident(g7,g6)
    c: Coincident(g7,g4)
    c: Coincident(g8,g5)
    c: Coincident(g9,g8)
    c: Coincident(g9,g2)
    c: Equal(g3,g2)
    c: Equal(g2,g6)
    c: Equal(g6,g5)
    c: Equal(g7,g4)
    c: Equal(g4,g9)
    c: Equal(g9,g8)
    c: Coincident(g10,g6)
    c: Coincident(g10,g5)
    c: Equal(g10,g8)
    c: Angle(g4,g3) = 2.0944
    c: Distance(g1) = 2
    c: Coincident(g11,g6)
    c: Coincident(g12,g5)
    c: Coincident(g13,g8)
    c: Horizontal(g13)
    c: Coincident(g14,g2)
    c: Coincident(g15,g3)
    c: Coincident(g16,g4)
    c: Equal(g15,g14)
    c: Equal(g14,g13)
    c: Equal(g13,g12)
    c: Equal(g12,g11)
    c: Distance(g15) = 1.5
    c: Coincident(g17,g12)
    c: Horizontal(g17)
    c: Coincident(g18,g11)
    c: Horizontal(g18)
    c: Coincident(g19,g18)
    c: Coincident(g19,g17)
    c: Horizontal(g19)
    c: Equal(g19,g7)
    c: Equal(g17,g18)
    c: Coincident(g20,g19)
    c: Coincident(g21,g20)
    c: Coincident(g22,g21)
    c: Horizontal(g22)
    c: Coincident(g23,g22)
    c: Coincident(g24,g23)
    c: Coincident(g24,g19)
    c: Equal(g20,g21)
    c: Equal(g21,g22)
    c: Equal(g22,g23)
    c: Equal(g23,g24)
    c: Equal(g24,g19)
    c: Angle(g19,g24) = 2.0944
    c: Angle(g24,g23) = 2.0944
    c: Coincident(g25,g12)
    c: Coincident(g26,g13)
    c: Coincident(g27,g26)
    c: Coincident(g27,g25)
    c: Parallel(g26,g8)
    c: Parallel(g27,g8)
    c: Parallel(g25,g8)
    c: Equal(g27,g8)
    c: Equal(g26,g25)
    c: Coincident(g28,g13)
    c: Coincident(g29,g14)
    c: Coincident(g30,g29)
    c: Coincident(g30,g28)
    c: Parallel(g29,g9)
    c: Parallel(g30,g9)
    c: Parallel(g28,g9)
    c: Equal(g30,g9)
    c: Equal(g28,g29)
    c: Coincident(g31,g15)
    c: Horizontal(g31)
    c: Coincident(g32,g14)
    c: Horizontal(g32)
    c: Coincident(g33,g31)
    c: Coincident(g33,g32)
    c: Horizontal(g33)
    c: Equal(g31,g32)
    c: Equal(g33,g4)
    c: Coincident(g34,g15)
    c: Coincident(g35,g16)
    c: Coincident(g36,g34)
    c: Coincident(g36,g35)
    c: Parallel(g35,g4)
    c: Parallel(g36,g4)
    c: Parallel(g4,g34)
    c: Equal(g34,g35)
    c: Equal(g36,g4)
    c: Coincident(g37,g27)
    c: Coincident(g38,g37)
    c: Horizontal(g38)
    c: Coincident(g39,g38)
    c: Coincident(g40,g39)
    c: Coincident(g41,g40)
    c: Coincident(g41,g27)
    c: Coincident(g42,g30)
    c: Coincident(g43,g42)
    c: Coincident(g44,g43)
    c: Coincident(g45,g44)
    c: Coincident(g46,g45)
    c: Coincident(g46,g30)
    c: Coincident(g47,g33)
    c: Coincident(g48,g47)
    c: Coincident(g49,g48)
    c: Coincident(g50,g49)
    c: Coincident(g51,g50)
    c: Coincident(g51,g33)
    c: Coincident(g52,g36)
    c: Horizontal(g52)
    c: Coincident(g53,g52)
    c: Coincident(g54,g53)
    c: Coincident(g55,g54)
    c: Coincident(g56,g55)
    c: Coincident(g56,g36)
    c: Coincident(g57,g16)
    c: Coincident(g58,g11)
    c: Coincident(g59,g57)
    c: Coincident(g59,g58)
    c: Parallel(g57,g7)
    c: Parallel(g59,g7)
    c: Parallel(g58,g7)
    c: Equal(g58,g57)
    c: Equal(g59,g7)
    c: Coincident(g60,g59)
    c: Coincident(g61,g60)
    c: Coincident(g62,g61)
    c: Coincident(g63,g62)
    c: Coincident(g64,g63)
    c: Coincident(g64,g59)
    c: Horizontal(g64)
    c: Horizontal(g42)
    c: Horizontal(g41)
    c: Equal(g46,g45)
    c: Equal(g45,g44)
    c: Equal(g44,g43)
    c: Equal(g43,g42)
    c: Equal(g42,g41)
    c: Equal(g41,g40)
    c: Equal(g40,g39)
    c: Equal(g39,g37)
    c: Equal(g37,g38)
    c: Equal(g38,g27)
    c: Equal(g27,g47)
    c: Equal(g47,g48)
    c: Equal(g48,g49)
    c: Equal(g49,g50)
    c: Equal(g50,g51)
    c: Equal(g51,g56)
    c: Equal(g56,g55)
    c: Equal(g55,g54)
    c: Equal(g54,g53)
    c: Equal(g53,g52)
    c: Equal(g52,g64)
    c: Equal(g64,g63)
    c: Equal(g63,g62)
    c: Equal(g62,g61)
    c: Equal(g61,g60)
    c: Parallel(g24,g56)
    c: Parallel(g56,g40)
    c: Parallel(g40,g44)
    c: Parallel(g44,g48)
    c: Horizontal(g49)
    c: Horizontal(g55)
    c: Parallel(g63,g46)
    c: Parallel(g46,g60)
    c: Parallel(g43,g47)
    c: Parallel(g47,g36)
FEATURE [PartDesign::Pad] Pad008
  BaseFeature = -> Pocket001
  Direction = (0,0,-1)
  Length = 3.8
  Length2 = 10
  Profile = -> Sketch011
  ReferenceAxis = -> Sketch011 [N_Axis]
  Type = 0
FEATURE [PartDesign::Pocket] Pocket002
  BaseFeature = -> Pad008
  Direction = (0,0,1)
  Length = 5
  Length2 = 5
  Profile = -> Sketch012
  ReferenceAxis = -> Sketch012 [N_Axis]
  Reversed = true
  Type = 0
FEATURE [PartDesign::Pocket] Pocket003  label="Lautsprecher_Loch"
  BaseFeature = -> Pocket002
  Direction = (0,0,1)
  Length = 5
  Length2 = 5
  Profile = -> Sketch013
  ReferenceAxis = -> Sketch013 [N_Axis]
  Type = 0
FEATURE [Sketcher::SketchObject] Sketch030
  FullyConstrained = false
  MapMode = 5
  Support = -> [XY_Plane002]
  sketch-geometry (23):
    g0: LineSegment StartX=0 StartY=-1.8e-15 StartZ=0 EndX=0 EndY=15 EndZ=0
    g1: LineSegment StartX=0 StartY=15 StartZ=0 EndX=6 EndY=15 EndZ=0
    g2: LineSegment StartX=6 StartY=15 StartZ=0 EndX=6 EndY=-1.8e-15 EndZ=0
    g3: ArcOfCircle CenterX=16.0123 CenterY=-5.18464 CenterZ=0 NormalX=0 NormalY=0 NormalZ=1 AngleXU=0 Radius=11.2751 StartAngle=2.66379 EndAngle=4.84503
    g4: LineSegment StartX=0 StartY=-1.8e-15 StartZ=0 EndX=6 EndY=-1.8e-15 EndZ=0
    g5: LineSegment StartX=17.5034 StartY=-16.3607 StartZ=0 EndX=17.5034 EndY=-17.3607 EndZ=0
    g6: ArcOfCircle CenterX=17.5735 CenterY=0.214034 CenterZ=0 NormalX=0 NormalY=0 NormalZ=1 AngleXU=0 Radius=17.5748 StartAngle=3.15377 EndAngle=4.7084
    g7: LineSegment StartX=6 StartY=-1.8e-15 StartZ=0 EndX=17.5034 EndY=-16.3607 EndZ=0
    g8: GeomPoint X=3 Y=15 Z=0
    g9: Circle CenterX=3 CenterY=11.5 CenterZ=0 NormalX=0 NormalY=0 NormalZ=1 AngleXU=0 Radius=1.5
    g10: Circle CenterX=3 CenterY=11.5 CenterZ=0 NormalX=0 NormalY=0 NormalZ=1 AngleXU=0 Radius=2.5
    g11: LineSegment StartX=3 StartY=15 StartZ=0 EndX=3 EndY=14 EndZ=0
    g12: LineSegment StartX=3 StartY=14 StartZ=0 EndX=3 EndY=11.5 EndZ=0
    g13: LineSegment StartX=0 StartY=9 StartZ=0 EndX=6 EndY=9 EndZ=0
    g14: LineSegment StartX=6 StartY=26 StartZ=0 EndX=0 EndY=26 EndZ=0
    g15: LineSegment StartX=6 StartY=15 StartZ=0 EndX=6 EndY=18 EndZ=0
    g16: LineSegment StartX=6 StartY=18 StartZ=0 EndX=4.2 EndY=18 EndZ=0
    g17: LineSegment StartX=4.2 StartY=18 StartZ=0 EndX=4.2 EndY=21 EndZ=0
    g18: LineSegment StartX=4.2 StartY=21 StartZ=0 EndX=6 EndY=21 EndZ=0
    g19: LineSegment StartX=6 StartY=21 StartZ=0 EndX=6 EndY=26 EndZ=0
    g20: LineSegment StartX=0 StartY=15 StartZ=0 EndX=0 EndY=18 EndZ=0
    g21: LineSegment StartX=0 StartY=21 StartZ=0 EndX=0 EndY=26 EndZ=0
    g22: LineSegment StartX=0 StartY=21 StartZ=0 EndX=0 EndY=18 EndZ=0
  constraints (60):
    c: Coincident(g0,g-1)
    c: PointOnObject(g0,g-2)
    c: Coincident(g1,g0)
    c: Horizontal(g1)
    c: DistanceX(g1,g1) = 6
    c: Coincident(g2,g1)
    c: Vertical(g2)
    c: Coincident(g3,g2)
    c: Coincident(g4,g0)
    c: Coincident(g4,g2)
    c: Horizontal(g4)
    c: Coincident(g5,g3)
    c: Coincident(g6,g0)
    c: Vertical(g5)
    c: Coincident(g6,g5)
    c: DistanceY(g5,g5) = 1
    c: Coincident(g7,g2)
    c: Coincident(g7,g3)
    c: Symmetric(g1,g0,g8)
    c: Radius(g9) = 1.5
    c: Coincident(g10,g9)
    c: Radius(g10) = 2.5
    c: Coincident(g11,g8)
    c: Vertical(g11)
    c: DistanceY(g11,g11) = 1
    c: Coincident(g12,g11)
    c: Coincident(g12,g9)
    c: Vertical(g12)
    c: PointOnObject(g11,g10)
    c: PointOnObject(g13,g0)
    c: PointOnObject(g13,g2)
    c: Horizontal(g13)
    c: Tangent(g13,g10)
    c: DistanceY(g2,g13) = 9
    c: Distance(g7) = 20
    c: PointOnObject(g14,g-2)
    c: Horizontal(g14)
    c: Coincident(g15,g2)
    c: Vertical(g15)
    c: Coincident(g16,g15)
    c: Horizontal(g16)
    c: Coincident(g17,g16)
    c: Vertical(g17)
    c: Coincident(g18,g17)
    c: Horizontal(g18)
    c: Coincident(g19,g18)
    c: Coincident(g19,g14)
    c: Vertical(g19)
    c: Equal(g18,g16)
    c: Coincident(g20,g0)
    c: PointOnObject(g20,g-2)
    c: PointOnObject(g21,g-2)
    c: Coincident(g21,g14)
    c: Equal(g19,g21)
    c: DistanceY(g17,g17) = 3
    c: DistanceY(g19,g19) = 5
    c: DistanceY(g15,g15) = 3
    c: Coincident(g22,g21)
    c: Coincident(g22,g20)
    c: Equal(g22,g17)
FEATURE [PartDesign::Pad] Pad013
  Direction = (0,0,1)
  Length = 6
  Length2 = 10
  Profile = -> Sketch030
  ReferenceAxis = -> Sketch030 [N_Axis]
  Type = 0
FEATURE [Sketcher::SketchObject] Sketch031
  ExternalGeometry = -> [Sketch030]
  FullyConstrained = true
  MapMode = 5
  Support = -> [XY_Plane002]
  sketch-geometry (8):
    g0: LineSegment StartX=0 StartY=15 StartZ=0 EndX=0 EndY=0 EndZ=0
    g1: GeomPoint X=3 Y=15 Z=0
    g2: LineSegment StartX=3 StartY=15 StartZ=0 EndX=3 EndY=14 EndZ=0
    g3: Circle CenterX=3 CenterY=11.5 CenterZ=0 NormalX=0 NormalY=0 NormalZ=1 AngleXU=0 Radius=1.5
    g4: Circle CenterX=3 CenterY=11.5 CenterZ=0 NormalX=0 NormalY=0 NormalZ=1 AngleXU=0 Radius=2.5
    g5: LineSegment StartX=3 StartY=14 StartZ=0 EndX=3 EndY=11.5 EndZ=0
    g6: LineSegment StartX=0 StartY=15 StartZ=0 EndX=3 EndY=15 EndZ=0
    g7: LineSegment StartX=3 StartY=15 StartZ=0 EndX=6 EndY=15 EndZ=0
  constraints (18):
    c: Coincident(g0,g-6)
    c: Coincident(g2,g1)
    c: Vertical(g2)
    c: Coincident(g4,g3)
    c: Radius(g3) = 1.5
    c: Radius(g4) = 2.5
    c: Coincident(g5,g2)
    c: Coincident(g5,g3)
    c: Vertical(g5)
    c: PointOnObject(g2,g4)
    c: DistanceY(g2,g2) = 1
    c: Coincident(g6,g0)
    c: Horizontal(g6)
    c: Coincident(g7,g6)
    c: Coincident(g7,g-3)
    c: Equal(g7,g6)
    c: Coincident(g0,g-7)
    c: Coincident(g1,g6)
FEATURE [PartDesign::Pocket] Pocket007
  BaseFeature = -> Pad013
  Direction = (0,0,-1)
  Length = 7
  Length2 = 5
  Profile = -> Sketch031
  ReferenceAxis = -> Sketch031 [N_Axis]
  Reversed = true
  Type = 0
FEATURE [PartDesign::Body] Body001  label="Abzug_body"
  Group = -> [Sketch030,Pad013,Sketch031,Pocket007]
  Origin = -> Origin002
  Placement = pos=(3,-11.5,3) rot=(0,1,0;3.14159rad)
  Tip = -> Pocket007
FEATURE [Part::Compound] Compound
  Links = -> [Body001]
  Placement = pos=(94.35,-37.5,0.8) rot=(0,0,-1;5.49779rad)
FEATURE [App::MeasureDistance] Distance  label="Distance: 15,00 mm"
  Distance = 15.0002
  P1 = (103.079,-23.0323,17.5)
  P2 = (103,-23,2.5)
FEATURE [PartDesign::Body] Body
  Group = -> [Sketch,Sketch001,Sketch002,Sketch003,Pad,Thickness,Sketch004,Pad001,Pad002,Pad003,Fillet,Pad004,Sketch005,Sketch006,Pad005,Sketch007,Pocket,Hole,Sketch010,Pocket001,Sketch011,Sketch012,Sketch013,Pad008,Pocket002,Sketch014,Pocket003,Pocket004,Sketch026,Pad011,Sketch027,Pad012,Sketch032,Sketch033,Pocket008,Pocket009,Fillet001,Fillet002,Fillet003,Sketch034,Pocket010,Sketch035,Pad014,Sketch036,+6 more]
  Origin = -> Origin
  Tip = -> Pocket013
FEATURE [Sketcher::SketchObject] Sketch014  label="IR-Receiverloch"
  AttachmentOffset = pos=(0,0,0.5) rot=(0,0,1;0rad)
  FullyConstrained = true
  MapMode = 5
  Placement = pos=(-0.5,0,0) rot=(0.57735,-0.57735,-0.57735;2.0944rad)
  Support = -> [Pocket004]
  sketch-geometry (4):
    g0: LineSegment StartX=36 StartY=0 StartZ=0 EndX=36 EndY=3.5 EndZ=0
    g1: LineSegment StartX=36 StartY=3.5 StartZ=0 EndX=30 EndY=3.5 EndZ=0
    g2: LineSegment StartX=30 StartY=3.5 StartZ=0 EndX=30 EndY=0 EndZ=0
    g3: LineSegment StartX=30 StartY=0 StartZ=0 EndX=36 EndY=0 EndZ=0
  constraints (12):
    c: Horizontal(g1)
    c: Coincident(g2,g1)
    c: Vertical(g2)
    c: Coincident(g3,g2)
    c: Coincident(g3,g0)
    c: Vertical(g0)
    c: Coincident(g0,g1)
    c: DistanceX(g3,g3) = 6
    c: DistanceY(g2,g2) = 3.5
    c: PointOnObject(g0,g-1)
    c: Horizontal(g3)
    c: DistanceX(g-1,g2) = 30
FEATURE [PartDesign::Pocket] Pocket004
  BaseFeature = -> Pocket003
  Direction = (1,0,0)
  Length = 5
  Length2 = 5
  Profile = -> Sketch014
  ReferenceAxis = -> Sketch014 [N_Axis]
  Type = 0
FEATURE [Sketcher::SketchObject] Sketch026
  ExternalGeometry = -> [Pocket004]
  FullyConstrained = false
  MapMode = 5
  Placement = pos=(0,0,17.5) rot=(1,0,0;3.14159rad)
  sketch-geometry (2):
    g0: Circle CenterX=94.4 CenterY=37.5 CenterZ=0 NormalX=0 NormalY=0 NormalZ=1 AngleXU=0 Radius=1.5
    g1: Circle CenterX=94.4 CenterY=37.5 CenterZ=0 NormalX=0 NormalY=0 NormalZ=1 AngleXU=0 Radius=2
  constraints (3):
    c: Coincident(g1,g0)
    c: Radius(g0) = 1.5
    c: Radius(g1) = 2
FEATURE [PartDesign::Pad] Pad011  label="Triggerbefestigung"
  BaseFeature = -> Pocket004
  Direction = (0,0,-1)
  Length = 13.5
  Length2 = 10
  Profile = -> Sketch026
  ReferenceAxis = -> Sketch026 [N_Axis]
  Type = 0
FEATURE [Sketcher::SketchObject] Sketch027
  ExternalGeometry = -> [Pad011]
  FullyConstrained = false
  MapMode = 5
  Placement = pos=(0,0,17.5) rot=(1,0,0;3.14159rad)
  Support = -> [Pocket004]
  sketch-geometry (8):
    g0: LineSegment StartX=81.4208 StartY=36.5 StartZ=0 EndX=85.5 EndY=32.1 EndZ=0
    g1: LineSegment StartX=85.5 StartY=32.1 StartZ=0 EndX=82.5667 EndY=29.3805 EndZ=0
    g2: LineSegment StartX=82.5667 StartY=29.3805 StartZ=0 EndX=78.4875 EndY=33.7805 EndZ=0
    g3: LineSegment StartX=78.4875 StartY=33.7805 StartZ=0 EndX=81.4208 EndY=36.5 EndZ=0
    g4: LineSegment StartX=97 StartY=27 StartZ=0 EndX=103 EndY=27 EndZ=0
    g5: LineSegment StartX=103 StartY=27 StartZ=0 EndX=103 EndY=23 EndZ=0
    g6: LineSegment StartX=103 StartY=23 StartZ=0 EndX=97 EndY=23 EndZ=0
    g7: LineSegment StartX=97 StartY=23 StartZ=0 EndX=97 EndY=27 EndZ=0
  constraints (20):
    c: Coincident(g0,g1)
    c: Coincident(g1,g2)
    c: Coincident(g2,g3)
    c: Coincident(g3,g0)
    c: Equal(g0,g2)
    c: Equal(g3,g1)
    c: Angle(g2,g3) = 1.5708
    c: Distance(g0) = 6
    c: Distance(g3) = 4
    c: Coincident(g4,g5)
    c: Coincident(g5,g6)
    c: Coincident(g6,g7)
    c: Coincident(g7,g4)
    c: Horizontal(g4)
    c: Horizontal(g6)
    c: Vertical(g5)
    c: Vertical(g7)
    c: Distance(g4) = 6
    c: Distance(g5) = 4
    c: DistanceX(g0,g6) = 11.5
FEATURE [PartDesign::Pad] Pad012  label="Knöpfe"
  BaseFeature = -> Pad011
  Direction = (0,0,-1)
  Length = 15
  Length2 = 10
  Profile = -> Sketch027
  ReferenceAxis = -> Sketch027 [N_Axis]
  Type = 0
FEATURE [App::Part] Part
  Group = -> [Body]
  Origin = -> Origin001
FEATURE [Sketcher::SketchObject] Sketch032
  FullyConstrained = false
  MapMode = 5
  Placement = pos=(19.4367,20.9651,0) rot=(0.874475,-0.342997,-0.342997;1.70453rad)
  Support = -> [Pad012]
  sketch-geometry (2):
    g0: ArcOfCircle CenterX=81.6681 CenterY=0.179607 CenterZ=0 NormalX=0 NormalY=0 NormalZ=1 AngleXU=0 Radius=2.01645 StartAngle=0.127828 EndAngle=3.01376
    g1: LineSegment StartX=79.6681 StartY=0.436665 StartZ=0 EndX=83.6681 EndY=0.436665 EndZ=0
  constraints (2):
    c: Coincident(g1,g0)
    c: Coincident(g1,g0)
FEATURE [Sketcher::SketchObject] Sketch033
  ExternalGeometry = -> [Pad012]
  FullyConstrained = true
  MapMode = 5
  Placement = pos=(97,0,0) rot=(0.57735,-0.57735,-0.57735;2.0944rad)
  Support = -> [Pad012]
  sketch-geometry (2):
    g0: ArcOfCircle CenterX=25 CenterY=1 CenterZ=0 NormalX=0 NormalY=0 NormalZ=1 AngleXU=0 Radius=2.5 StartAngle=0.643501 EndAngle=2.49809
    g1: LineSegment StartX=23 StartY=2.5 StartZ=0 EndX=27 EndY=2.5 EndZ=0
  constraints (5):
    c: Coincident(g0,g-3)
    c: Coincident(g0,g-3)
    c: Diameter(g0) = 5
    c: Coincident(g1,g0)
    c: Coincident(g1,g0)
FEATURE [PartDesign::Pocket] Pocket008
  BaseFeature = -> Pad012
  Direction = (0.679869,0.733333,0)
  Length = 6
  Length2 = 5
  Profile = -> Sketch032
  ReferenceAxis = -> Sketch032 [N_Axis]
  Type = 0
FEATURE [PartDesign::Pocket] Pocket009
  BaseFeature = -> Pocket008
  Direction = (1,0,0)
  Length = 6
  Length2 = 5
  Profile = -> Sketch033
  ReferenceAxis = -> Sketch033 [N_Axis]
  Type = 0
FEATURE [PartDesign::Fillet] Fillet001
  Base = -> Pocket009 [Edge189,Edge191,Edge183]
  BaseFeature = -> Pocket009
  Radius = 1
  SupportTransform = false
  UseAllEdges = false
FEATURE [PartDesign::Fillet] Fillet002
  Base = -> Fillet001 [Edge162,Edge3]
  BaseFeature = -> Fillet001
  Radius = 5
  SupportTransform = false
  UseAllEdges = false
FEATURE [PartDesign::Fillet] Fillet003
  Base = -> Fillet002 [Edge4,Edge24,Edge34,Edge28,Edge29,Edge31]
  BaseFeature = -> Fillet002
  Radius = 3
  SupportTransform = false
  UseAllEdges = false
FEATURE [Sketcher::SketchObject] Sketch034
  ExternalGeometry = -> [Fillet003]
  FullyConstrained = true
  MapMode = 5
  Placement = pos=(159.421,37.9573,0) rot=(0.667,-0.526836,-0.526836;1.96513rad)
  Support = -> [Fillet003]
  sketch-geometry (6):
    g0: LineSegment StartX=53.0101 StartY=17 StartZ=0 EndX=67.0101 EndY=17 EndZ=0
    g1: LineSegment StartX=67.0101 StartY=17 StartZ=0 EndX=67.0101 EndY=13.5 EndZ=0
    g2: LineSegment StartX=67.0101 StartY=13.5 StartZ=0 EndX=53.0101 EndY=13.5 EndZ=0
    g3: LineSegment StartX=53.0101 StartY=13.5 StartZ=0 EndX=53.0101 EndY=17 EndZ=0
    g4: GeomPoint X=60.0101 Y=17.5 Z=0
    g5: LineSegment StartX=60.0101 StartY=17.5 StartZ=0 EndX=60.0101 EndY=17 EndZ=0
  constraints (15):
    c: Coincident(g0,g1)
    c: Coincident(g1,g2)
    c: Coincident(g2,g3)
    c: Coincident(g3,g0)
    c: Horizontal(g0)
    c: Horizontal(g2)
    c: Vertical(g1)
    c: Vertical(g3)
    c: Distance(g0,g-3) = 0.5
    c: DistanceY(g3,g3) = 3.5
    c: DistanceX(g0,g0) = 14
    c: Symmetric(g-3,g-3,g4)
    c: Coincident(g5,g4)
    c: Vertical(g5)
    c: Symmetric(g0,g0,g5)
FEATURE [PartDesign::Pocket] Pocket010
  BaseFeature = -> Fillet003
  Direction = (0.972806,0.231621,0)
  Length = 5
  Length2 = 5
  Profile = -> Sketch034
  ReferenceAxis = -> Sketch034 [N_Axis]
  Type = 0
FEATURE [Sketcher::SketchObject] Sketch035
  ExternalGeometry = -> [Pocket010]
  FullyConstrained = true
  MapMode = 5
  Placement = pos=(0,0,17.5) rot=(1,0,0;3.14159rad)
  Support = -> [Pocket010]
  sketch-geometry (5):
    g0: LineSegment StartX=147.056 StartY=24.8061 StartZ=0 EndX=154.056 EndY=24.8061 EndZ=0
    g1: LineSegment StartX=154.056 StartY=24.8061 StartZ=0 EndX=154.056 EndY=17.8061 EndZ=0
    g2: LineSegment StartX=154.056 StartY=17.8061 StartZ=0 EndX=147.056 EndY=17.8061 EndZ=0
    g3: LineSegment StartX=147.056 StartY=17.8061 StartZ=0 EndX=147.056 EndY=24.8061 EndZ=0
    g4: GeomPoint X=147.056 Y=21.3061 Z=0
  constraints (12):
    c: Coincident(g0,g1)
    c: Coincident(g1,g2)
    c: Coincident(g2,g3)
    c: Coincident(g3,g0)
    c: Horizontal(g0)
    c: Horizontal(g2)
    c: Vertical(g1)
    c: Vertical(g3)
    c: Equal(g0,g1)
    c: Symmetric(g2,g0,g4)
    c: Coincident(g4,g-4)
    c: DistanceY(g1,g1) = 7
FEATURE [PartDesign::Pad] Pad014
  BaseFeature = -> Pocket010
  Direction = (0,0,-1)
  Length = 6
  Length2 = 10
  Profile = -> Sketch035
  ReferenceAxis = -> Sketch035 [N_Axis]
  Type = 0
FEATURE [Sketcher::SketchObject] Sketch036
  ExternalGeometry = -> [Pad014]
  FullyConstrained = true
  MapMode = 5
  Placement = pos=(0,-24.8061,0) rot=(1,0,0;1.5708rad)
  Support = -> [Pad014]
  sketch-geometry (4):
    g0: LineSegment StartX=154.056 StartY=14 StartZ=0 EndX=150.556 EndY=14 EndZ=0
    g1: LineSegment StartX=150.556 StartY=14 StartZ=0 EndX=150.556 EndY=17.5 EndZ=0
    g2: LineSegment StartX=150.556 StartY=17.5 StartZ=0 EndX=154.056 EndY=17.5 EndZ=0
    g3: LineSegment StartX=154.056 StartY=17.5 StartZ=0 EndX=154.056 EndY=14 EndZ=0
  constraints (12):
    c: Coincident(g0,g1)
    c: Coincident(g1,g2)
    c: Coincident(g2,g3)
    c: Coincident(g3,g0)
    c: Horizontal(g0)
    c: Horizontal(g2)
    c: Vertical(g1)
    c: Vertical(g3)
    c: PointOnObject(g0,g-5)
    c: DistanceY(g3,g3) = 3.5
    c: PointOnObject(g1,g-3)
    c: Equal(g3,g0)
FEATURE [PartDesign::Pocket] Pocket011
  BaseFeature = -> Pad014
  Direction = (0,1,-2e-16)
  Length = 7
  Length2 = 5
  Profile = -> Sketch036
  ReferenceAxis = -> Sketch036 [N_Axis]
  Type = 0
FEATURE [PartDesign::Pocket] Pocket012
  BaseFeature = -> Pocket011
  Direction = (0,0,1)
  Length = 5
  Length2 = 5
  Profile = -> Pocket010 [Face212,Face211,Face214,Face210,Face209,Face208]
  Type = 0
FEATURE [Sketcher::SketchObject] Sketch037
  ExternalGeometry = -> [Pocket012]
  FullyConstrained = true
  MapMode = 5
  Placement = pos=(0,0,4) rot=(1,0,0;3.14159rad)
  Support = -> [Pocket012]
  sketch-geometry (2):
    g0: Circle CenterX=94.4 CenterY=37.5 CenterZ=0 NormalX=0 NormalY=0 NormalZ=1 AngleXU=0 Radius=3
    g1: Circle CenterX=94.4 CenterY=37.5 CenterZ=0 NormalX=0 NormalY=0 NormalZ=1 AngleXU=0 Radius=1.5
  constraints (4):
    c: Coincident(g1,g0)
    c: Equal(g1,g-3)
    c: Diameter(g0) = 6
    c: Coincident(g0,g-4)
FEATURE [PartDesign::Pad] Pad015
  BaseFeature = -> Pocket012
  Direction = (0,0,-1)
  Length = 14
  Length2 = 10
  Profile = -> Sketch037
  ReferenceAxis = -> Sketch037 [N_Axis]
  Reversed = true
  Type = 0
FEATURE [Sketcher::SketchObject] Sketch038
  ExternalGeometry = -> [Sketch027,Pocket009]
  FullyConstrained = true
  MapMode = 5
  Placement = pos=(103,0,0) rot=(0.57735,0.57735,0.57735;2.0944rad)
  Support = -> [Pocket009]
  sketch-geometry (4):
    g0: LineSegment StartX=-23 StartY=16 StartZ=0 EndX=-23 EndY=2.5 EndZ=0
    g1: LineSegment StartX=-23 StartY=2.5 StartZ=0 EndX=-27 EndY=2.5 EndZ=0
    g2: LineSegment StartX=-27 StartY=2.5 StartZ=0 EndX=-27 EndY=16 EndZ=0
    g3: LineSegment StartX=-27 StartY=16 StartZ=0 EndX=-23 EndY=16 EndZ=0
  constraints (11):
    c: Coincident(g0,g1)
    c: Coincident(g1,g2)
    c: Horizontal(g1)
    c: Vertical(g0)
    c: Vertical(g2)
    c: Coincident(g0,g-6)
    c: Coincident(g3,g2)
    c: Coincident(g3,g0)
    c: Horizontal(g3)
    c: DistanceY(g2,g-4) = 1.5
    c: PointOnObject(g2,g-4)
FEATURE [PartDesign::Pocket] Pocket013
  BaseFeature = -> Pad015
  Direction = (-1,0,0)
  Length = 6
  Length2 = 5
  Profile = -> Sketch038
  ReferenceAxis = -> Sketch038 [N_Axis]
  Type = 0
